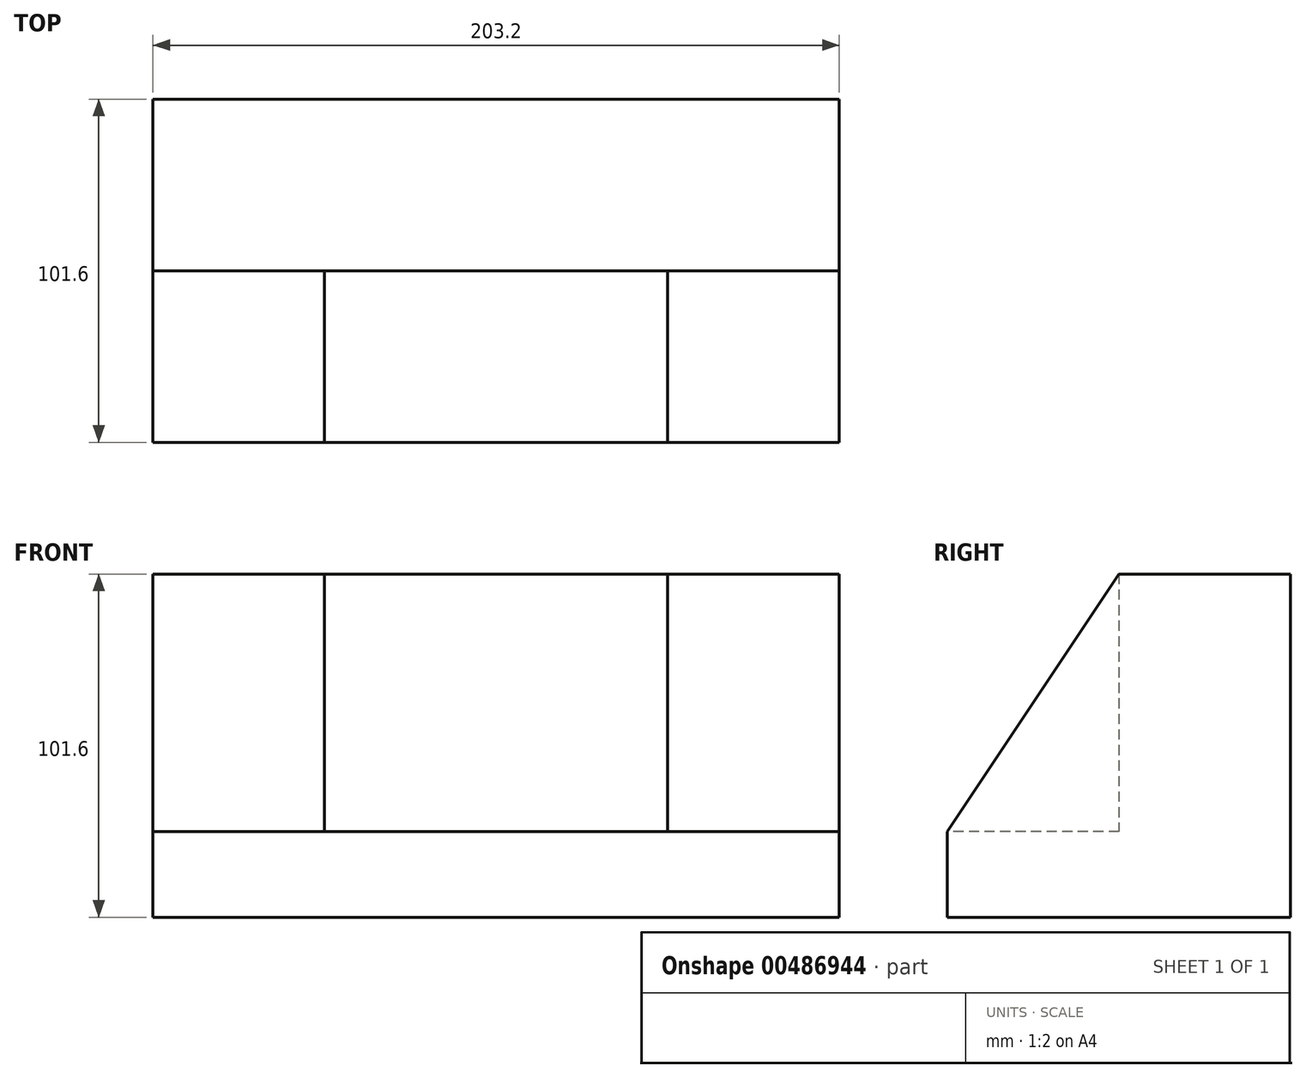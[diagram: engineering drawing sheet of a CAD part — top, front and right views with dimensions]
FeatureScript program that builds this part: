
annotation { "Feature Type Name" : "Feature", "Feature Type Description" : "" }
export const myFeature = defineFeature(function(context is Context, id is Id, definition is map)
    precondition{}
    {
        {
            var Q0;
            Q0=qCreatedBy(makeId("Front.planeOp"),FACE);
            var sketch = newSketch(context, id + "F0", { "sketchPlane" : qUnion([Q0])});
            skLineSegment(sketch, "E0.bottom", {"start": v(-101.6, 50.8) * mm, "end": v(101.6, 50.8) * mm});
            skLineSegment(sketch, "E0.top", {"start": v(-101.6, -50.8) * mm, "end": v(101.6, -50.8) * mm});
            skLineSegment(sketch, "E0.left", {"start": v(-101.6, 50.8) * mm, "end": v(-101.6, -50.8) * mm});
            skLineSegment(sketch, "E0.right", {"start": v(101.6, 50.8) * mm, "end": v(101.6, -50.8) * mm});
            skPoint(sketch, "E0.middle", {"position": v(0, 0) * mm});
            skSolve(sketch);
        }
        {
            var Q0;
            Q0 = qSketchRegion(id + "F0", true);
            extrude(context, id + "F1", {"entities" : qUnion([Q0]), "depth" : 101.6 * mm});
        }
        {
            var Q0;
            Q0=makeQuery(id+"F1.opExtrude","CAP_FACE",FACE,{"disambiguationData":[OSD([sQuery(id+"F0.wireOp",EDGE,"E0.bottom"),sQuery(id+"F0.wireOp",EDGE,"E0.top"),sQuery(id+"F0.wireOp",EDGE,"E0.left"),sQuery(id+"F0.wireOp",EDGE,"E0.right")])],"isStart":false});
            var sketch = newSketch(context, id + "F2", { "sketchPlane" : qUnion([Q0])});
            skLineSegment(sketch, "E1.bottom", {"start": v(-50.8, 50.8) * mm, "end": v(50.8, 50.8) * mm});
            skLineSegment(sketch, "E1.top", {"start": v(-50.8, -25.4) * mm, "end": v(50.8, -25.4) * mm});
            skLineSegment(sketch, "E1.left", {"start": v(-50.8, 50.8) * mm, "end": v(-50.8, -25.4) * mm});
            skLineSegment(sketch, "E1.right", {"start": v(50.8, 50.8) * mm, "end": v(50.8, -25.4) * mm});
            skPoint(sketch, "E1.middle", {"position": v(0, 12.7) * mm});
            skSolve(sketch);
        }
        {
            var Q0;
            Q0 = qSketchRegion(id + "F2", true);
            extrude(context, id + "F3", {"entities" : qUnion([Q0]), "operationType" : NewBodyOperationType.REMOVE, "oppositeDirection" : true, "depth" : 50.8 * mm});
        }
        {
            var Q0;
            Q0=makeQuery(id+"F3.boolean.opBoolean","COPY",FACE,{"derivedFrom":makeQuery(id+"F3.opExtrude","SWEPT_FACE",FACE,{"disambiguationData":[OSD([sQuery(id+"F2.wireOp",EDGE,"E1.left")])]})});
            var sketch = newSketch(context, id + "F4", { "sketchPlane" : qUnion([Q0])});
            skLineSegment(sketch, "E2", {"start": v(-50.8, 50.8) * mm, "end": v(-101.6, -25.4) * mm});
            skLineSegment(sketch, "E3", {"start": v(-101.6, -25.4) * mm, "end": v(-101.6, 50.8) * mm});
            skLineSegment(sketch, "E4", {"start": v(-101.6, 50.8) * mm, "end": v(-50.8, 50.8) * mm});
            skSolve(sketch);
        }
        {
            var Q0;
            Q0 = qSketchRegion(id + "F4", true);
            extrude(context, id + "F5", {"entities" : qUnion([Q0]), "operationType" : NewBodyOperationType.REMOVE, "oppositeDirection" : true, "depth" : 50.8 * mm});
        }
        {
            var Q0;
            Q0=makeQuery(id+"F3.boolean.opBoolean","COPY",FACE,{"derivedFrom":makeQuery(id+"F3.opExtrude","SWEPT_FACE",FACE,{"disambiguationData":[OSD([sQuery(id+"F2.wireOp",EDGE,"E1.right")])]})});
            var sketch = newSketch(context, id + "F6", { "sketchPlane" : qUnion([Q0])});
            skLineSegment(sketch, "E5", {"start": v(50.8, 50.8) * mm, "end": v(101.6, -25.4) * mm});
            skLineSegment(sketch, "E6", {"start": v(101.6, -25.4) * mm, "end": v(101.6, 50.8) * mm});
            skLineSegment(sketch, "E7", {"start": v(101.6, 50.8) * mm, "end": v(50.8, 50.8) * mm});
            skSolve(sketch);
        }
        {
            var Q0;
            Q0 = qSketchRegion(id + "F6", true);
            extrude(context, id + "F7", {"entities" : qUnion([Q0]), "operationType" : NewBodyOperationType.REMOVE, "oppositeDirection" : true, "depth" : 50.8 * mm});
        }
    });
